# Revit family: Furniture_GroheLimited_EssentialsTowelRail800mm_40386000_METRICa
name_source: partatom
category: Furniture
revit_build: Autodesk Revit 2015 (Build: 20160512_0715(x64)
units: mm (PartAtom-declared; Revit-internal decimal feet)

## types (9) — shared parameters
ADACompliant = No
Assembly Code = C1030220
AssetType = Fixed
BIMObjectName = Furniture_GroheLimited_EssentialsTowelRail800mm_40386000_METRIC
ClassificationName = Uniclass2015
ClassificationValue = Pr_40_20_76_90
Description = 800mm Grohe Essentials Towel Rail
DurationUnit = Years
Ecojoy = No
Features = 800mm Grohe Essentials Towel Rail
Height = 60 mm  [stored 0.19685 ft]
IfcExportAs = IfcPipeFitting
IfcExportType = IfcPipeFittingType
Keynote = N13
Length = 854 mm  [stored 2.80184 ft]
LowEmittingMaterial = No
Manufacturer = Grohe Limited
ManufacturerName = Grohe Limited
MasterformatNumber = 22 41 39
MasterformatTitle = Residential Faucets, Supplies, and Trim
Model = Essentials Towel Rail
ModelReference = Essentials Towel Rail
NBSDescription = Towel rails
NBSObjectName = Grohe Limited - Towel rails
NBSReference = 45-35-72/372
NominalDepth = 54 mm  [stored 0.177165 ft]
NominalHeight = 60 mm  [stored 0.19685 ft]
NominalLength = 854 mm  [stored 2.80184 ft]
ProductDocumentationLink = http://www.grohe.co.uk
ProductPageURL = http://www.grohe.co.uk
ProductionYear = 2017
TypeName = Essentials Towel Rail
URL = www.grohe.com
WarrantyDurationUnit = Years
Width = 54 mm  [stored 0.177165 ft]
_BSBibleVersion = 14
_CurrentRevision = 1
_DistributedBy = www.bimstore.co.uk
zero-valued in all types: Cost, Default Elevation, ExpectedLife, _BimSpecGuid

## per-type parameters (varying)
| type | Color | Finish | Material | PrimaryMaterial |
| 40386000 | Chrome | Chrome | Chrome | GroheLimited-Chorme |
| 40386A01 | Hard Graphite | Hard Graphite | Hard Graphite | GroheLimited-HardGraphite |
| 40386AL1 | Brushed Hard Graphite | Brushed Hard Graphite | Brushed Hard Graphite | GroheLimited-BrushedHardGraphite |
| 40386BE1 | Nickel | Nickel | Nickel | GroheLimited-Nickel |
| 40386DA1 | Warm Sunset | Warm Sunset | Warm Sunset | GroheLimited-WarmSunset |
| 40386DL1 | Brushed Warm Sunset | Brushed Warm Sunset | Brushed Warm Sunset | GroheLimited-BrushedWarmSunset |
| 40386EN1 | Brushed Nickel | Brushed Nickel | Brushed Nickel | GroheLimited-BrushedNickel |
| 40386GL1 | Cool Sunrise | Cool Sunrise | Cool Sunrise | GroheLimited-CoolSunrise |
| 40386GN1 | Brushed Cool Sunrise | Brushed Cool Sunrise | Brushed Cool Sunrise | GroheLimited-BrushedCoolSunrise |

note: column(s) folded — value = type name in every type: ModelNumber, Type Comments

note: [stored X ft] marks values corroborated as IEEE doubles in the binary element streams (Revit-internal decimal feet)

## geometry (parser evidence)
native form markers: Blend x2, Sweep x2
no freeform markers — native parametric forms only
